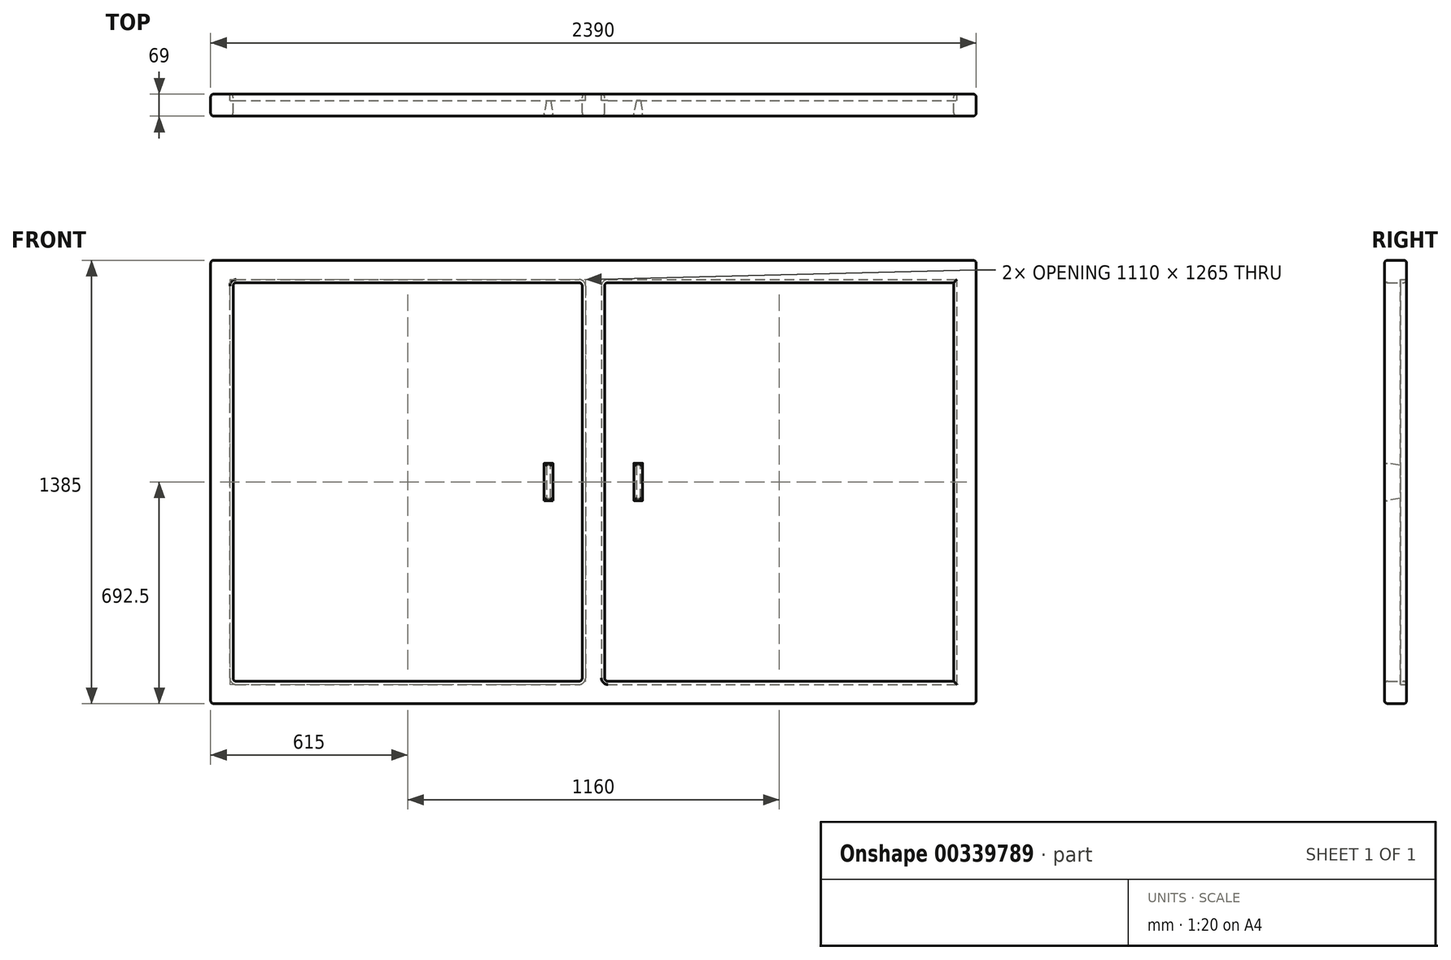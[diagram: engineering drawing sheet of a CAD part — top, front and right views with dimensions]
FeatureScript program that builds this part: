
annotation { "Feature Type Name" : "Feature", "Feature Type Description" : "" }
export const myFeature = defineFeature(function(context is Context, id is Id, definition is map)
    precondition{}
    {
        {
            var Q0;
            Q0=qCreatedBy(makeId("Front.planeOp"),FACE);
            var sketch = newSketch(context, id + "F0", { "sketchPlane" : qUnion([Q0])});
            skLineSegment(sketch, "E0.bottom", {"start": v(0, 0) * mm, "end": v(2390, 0) * mm});
            skLineSegment(sketch, "E0.top", {"start": v(0, 1385) * mm, "end": v(2390, 1385) * mm});
            skLineSegment(sketch, "E0.left", {"start": v(0, 0) * mm, "end": v(0, 1385) * mm});
            skLineSegment(sketch, "E0.right", {"start": v(2390, 0) * mm, "end": v(2390, 1385) * mm});
            skLineSegment(sketch, "E1.0", {"start": v(70, 1315) * mm, "end": v(1160, 1315) * mm});
            skLineSegment(sketch, "E1.1", {"start": v(70, 70) * mm, "end": v(70, 1315) * mm});
            skLineSegment(sketch, "E1.2", {"start": v(70, 70) * mm, "end": v(1160, 70) * mm});
            skLineSegment(sketch, "E1.3", {"start": v(2320, 70) * mm, "end": v(2320, 1315) * mm});
            skLineSegment(sketch, "E2.0", {"start": v(1160, 1315) * mm, "end": v(1160, 70) * mm});
            skLineSegment(sketch, "E3.0", {"start": v(1230, 1315) * mm, "end": v(1230, 70) * mm});
            skPoint(sketch, "E4.end.orphan", {"position": v(1195, 70) * mm});
            skPoint(sketch, "E4.start.orphan", {"position": v(1195, 1315) * mm});
            skLineSegment(sketch, "E5.trimOffspring", {"start": v(1230, 1315) * mm, "end": v(2320, 1315) * mm});
            skLineSegment(sketch, "E6.trimOffspring", {"start": v(1230, 70) * mm, "end": v(2320, 70) * mm});
            skSolve(sketch);
        }
        {
            var Q0;
            Q0=makeQuery(id+"F0.imprint","IMPRINT",FACE,{"disambiguationData":[TD([[makeQuery(id+"F0.imprint","IMPRINT",EDGE,{"derivedFrom":sQuery(id+"F0.wireOp",EDGE,"E0.bottom")}),1.0]])]});
            extrude(context, id + "F1", {"entities" : qUnion([Q0]), "depth" : 69 * mm});
        }
        {
            var Q0;
            Q0=makeQuery(id+"F1.opExtrude","CAP_FACE",FACE,{"disambiguationData":[OSD([sQuery(id+"F0.wireOp",EDGE,"E0.bottom"),sQuery(id+"F0.wireOp",EDGE,"E0.top"),sQuery(id+"F0.wireOp",EDGE,"E0.left"),sQuery(id+"F0.wireOp",EDGE,"E0.right"),sQuery(id+"F0.wireOp",EDGE,"E1.0"),sQuery(id+"F0.wireOp",EDGE,"E1.1"),sQuery(id+"F0.wireOp",EDGE,"E1.2"),sQuery(id+"F0.wireOp",EDGE,"E1.3"),sQuery(id+"F0.wireOp",EDGE,"E2.0"),sQuery(id+"F0.wireOp",EDGE,"E3.0"),sQuery(id+"F0.wireOp",EDGE,"E5.trimOffspring"),sQuery(id+"F0.wireOp",EDGE,"E6.trimOffspring")])],"isStart":false});
            var Q1;
            Q1=makeQuery(id+"F1.opExtrude","CAP_FACE",FACE,{"disambiguationData":[OSD([sQuery(id+"F0.wireOp",EDGE,"E0.bottom"),sQuery(id+"F0.wireOp",EDGE,"E0.top"),sQuery(id+"F0.wireOp",EDGE,"E0.left"),sQuery(id+"F0.wireOp",EDGE,"E0.right"),sQuery(id+"F0.wireOp",EDGE,"E1.0"),sQuery(id+"F0.wireOp",EDGE,"E1.1"),sQuery(id+"F0.wireOp",EDGE,"E1.2"),sQuery(id+"F0.wireOp",EDGE,"E1.3"),sQuery(id+"F0.wireOp",EDGE,"E2.0"),sQuery(id+"F0.wireOp",EDGE,"E3.0"),sQuery(id+"F0.wireOp",EDGE,"E5.trimOffspring"),sQuery(id+"F0.wireOp",EDGE,"E6.trimOffspring")])],"isStart":true});
            var Q2;
            Q2=makeQuery(id+"F1.opExtrude","SWEPT_FACE",FACE,{"disambiguationData":[OSD([sQuery(id+"F0.wireOp",EDGE,"E0.top")])]});
            var Q3;
            Q3=makeQuery(id+"F1.opExtrude","SWEPT_FACE",FACE,{"disambiguationData":[OSD([sQuery(id+"F0.wireOp",EDGE,"E0.right")])]});
            var Q4;
            Q4=makeQuery(id+"F1.opExtrude","SWEPT_FACE",FACE,{"disambiguationData":[OSD([sQuery(id+"F0.wireOp",EDGE,"E1.2")])]});
            var Q5;
            Q5=makeQuery(id+"F1.opExtrude","SWEPT_FACE",FACE,{"disambiguationData":[OSD([sQuery(id+"F0.wireOp",EDGE,"E3.0")])]});
            var Q6;
            Q6=makeQuery(id+"F1.opExtrude","SWEPT_FACE",FACE,{"disambiguationData":[OSD([sQuery(id+"F0.wireOp",EDGE,"E0.bottom")])]});
            var Q7;
            Q7=makeQuery(id+"F1.opExtrude","SWEPT_EDGE",EDGE,{"disambiguationData":[OSD([sQuery(id+"F0.wireOp",EDGE,"E1.0"),sQuery(id+"F0.wireOp",EDGE,"E2.0")])]});
            var Q8;
            Q8=makeQuery(id+"F1.opExtrude","SWEPT_EDGE",EDGE,{"disambiguationData":[OSD([sQuery(id+"F0.wireOp",EDGE,"E1.0"),sQuery(id+"F0.wireOp",EDGE,"E1.1")])]});
            fillet(context, id + "F2", {"entities" : qUnion([Q0, Q1, Q2, Q3, Q4, Q5, Q6, Q7, Q8]), "radius" : 10 * mm, "tangentPropagation" : true, "allowEdgeOverflow" : false});
        }
        {
            var Q0;
            Q0=qCreatedBy(makeId("Front.planeOp"),FACE);
            var sketch = newSketch(context, id + "F3", { "sketchPlane" : qUnion([Q0])});
            skLineSegment(sketch, "E7.0", {"start": v(1320, 632.5) * mm, "end": v(1320, 752.5) * mm});
            skLineSegment(sketch, "E8", {"start": v(1320, 692.5) * mm, "end": v(1320, 752.5) * mm});
            skLineSegment(sketch, "E9", {"start": v(1320, 752.5) * mm, "end": v(1350, 752.5) * mm});
            skLineSegment(sketch, "E10", {"start": v(1350, 752.5) * mm, "end": v(1350, 632.5) * mm});
            skLineSegment(sketch, "E11", {"start": v(1350, 632.5) * mm, "end": v(1320, 632.5) * mm});
            skLineSegment(sketch, "E12.0", {"start": v(5, 5) * mm, "end": v(2385, 5) * mm});
            skLineSegment(sketch, "E12.1", {"start": v(5, 1380) * mm, "end": v(5, 5) * mm});
            skLineSegment(sketch, "E12.2", {"start": v(2385, 1380) * mm, "end": v(5, 1380) * mm});
            skLineSegment(sketch, "E12.3", {"start": v(2385, 5) * mm, "end": v(2385, 1380) * mm});
            skLineSegment(sketch, "E13.0", {"start": v(1195, 1305) * mm, "end": v(1195, 80) * mm});
            skPoint(sketch, "E14.orphan", {"position": v(1320, 1305) * mm});
            skPoint(sketch, "E15.orphan", {"position": v(1320, 80) * mm});
            skLineSegment(sketch, "E16.MirrorCS", {"start": v(1070, 692.5) * mm, "end": v(1070, 752.5) * mm});
            skLineSegment(sketch, "E17.MirrorCS", {"start": v(1070, 632.5) * mm, "end": v(1070, 752.5) * mm});
            skLineSegment(sketch, "E18.MirrorCS", {"start": v(1040, 632.5) * mm, "end": v(1070, 632.5) * mm});
            skLineSegment(sketch, "E19.MirrorCS", {"start": v(1040, 752.5) * mm, "end": v(1040, 632.5) * mm});
            skLineSegment(sketch, "E20.MirrorCS", {"start": v(1070, 752.5) * mm, "end": v(1040, 752.5) * mm});
            skSolve(sketch);
        }
        {
            var Q0;
            Q0=makeQuery(id+"F1.opExtrude","CAP_FACE",FACE,{"disambiguationData":[OSD([sQuery(id+"F0.wireOp",EDGE,"E0.bottom"),sQuery(id+"F0.wireOp",EDGE,"E0.top"),sQuery(id+"F0.wireOp",EDGE,"E0.left"),sQuery(id+"F0.wireOp",EDGE,"E0.right"),sQuery(id+"F0.wireOp",EDGE,"E1.0"),sQuery(id+"F0.wireOp",EDGE,"E1.1"),sQuery(id+"F0.wireOp",EDGE,"E1.2"),sQuery(id+"F0.wireOp",EDGE,"E1.3"),sQuery(id+"F0.wireOp",EDGE,"E2.0"),sQuery(id+"F0.wireOp",EDGE,"E3.0"),sQuery(id+"F0.wireOp",EDGE,"E5.trimOffspring"),sQuery(id+"F0.wireOp",EDGE,"E6.trimOffspring")])],"isStart":true});
            var sketch = newSketch(context, id + "F4", { "sketchPlane" : qUnion([Q0])});
            skLineSegment(sketch, "E21.0", {"start": v(-2330, 60) * mm, "end": v(-2330, 1325) * mm});
            skArc(sketch, "E21.1", {"start": v(-1220, 1305) * mm, "mid": v(-1225.86, 1319.14) * mm, "end": v(-1240, 1325) * mm});
            skLineSegment(sketch, "E21.2", {"start": v(-1220, 1305) * mm, "end": v(-1220, 80) * mm});
            skLineSegment(sketch, "E21.3", {"start": v(-2330, 1325) * mm, "end": v(-1240, 1325) * mm});
            skArc(sketch, "E21.4", {"start": v(-1240, 60) * mm, "mid": v(-1225.86, 65.86) * mm, "end": v(-1220, 80) * mm});
            skLineSegment(sketch, "E21.5", {"start": v(-1240, 60) * mm, "end": v(-2330, 60) * mm});
            skArc(sketch, "E22.0", {"start": v(-1150, 1325) * mm, "mid": v(-1164.14, 1319.14) * mm, "end": v(-1170, 1305) * mm});
            skLineSegment(sketch, "E22.1", {"start": v(-1170, 80) * mm, "end": v(-1170, 1305) * mm});
            skLineSegment(sketch, "E22.2", {"start": v(-1150, 1325) * mm, "end": v(-80, 1325) * mm});
            skArc(sketch, "E22.3", {"start": v(-1170, 80) * mm, "mid": v(-1164.14, 65.86) * mm, "end": v(-1150, 60) * mm});
            skArc(sketch, "E22.4", {"start": v(-60, 1305) * mm, "mid": v(-65.86, 1319.14) * mm, "end": v(-80, 1325) * mm});
            skLineSegment(sketch, "E22.5", {"start": v(-60, 1305) * mm, "end": v(-60, 80) * mm});
            skArc(sketch, "E22.6", {"start": v(-80, 60) * mm, "mid": v(-65.86, 65.86) * mm, "end": v(-60, 80) * mm});
            skLineSegment(sketch, "E22.7", {"start": v(-80, 60) * mm, "end": v(-1150, 60) * mm});
            skSolve(sketch);
        }
        {
            var Q0;
            Q0 = qSketchRegion(id + "F4", true);
            extrude(context, id + "F5", {"entities" : qUnion([Q0]), "oppositeDirection" : true, "depth" : 20 * mm});
        }
        {
            var Q0;
            Q0=makeQuery(id+"F1.opExtrude","CAP_FACE",FACE,{"disambiguationData":[OSD([sQuery(id+"F0.wireOp",EDGE,"E0.bottom"),sQuery(id+"F0.wireOp",EDGE,"E0.top"),sQuery(id+"F0.wireOp",EDGE,"E0.left"),sQuery(id+"F0.wireOp",EDGE,"E0.right"),sQuery(id+"F0.wireOp",EDGE,"E1.0"),sQuery(id+"F0.wireOp",EDGE,"E1.1"),sQuery(id+"F0.wireOp",EDGE,"E1.2"),sQuery(id+"F0.wireOp",EDGE,"E1.3"),sQuery(id+"F0.wireOp",EDGE,"E2.0"),sQuery(id+"F0.wireOp",EDGE,"E3.0"),sQuery(id+"F0.wireOp",EDGE,"E5.trimOffspring"),sQuery(id+"F0.wireOp",EDGE,"E6.trimOffspring")])],"isStart":false});
            var sketch = newSketch(context, id + "F6", { "sketchPlane" : qUnion([Q0])});
            skLineSegment(sketch, "E23.0", {"start": v(1350, 632.5) * mm, "end": v(1350, 752.5) * mm});
            skLineSegment(sketch, "E23.1", {"start": v(1320, 632.5) * mm, "end": v(1350, 632.5) * mm});
            skLineSegment(sketch, "E23.2", {"start": v(1350, 752.5) * mm, "end": v(1320, 752.5) * mm});
            skLineSegment(sketch, "E23.3", {"start": v(1320, 752.5) * mm, "end": v(1320, 692.5) * mm});
            skLineSegment(sketch, "E23.4", {"start": v(1320, 692.5) * mm, "end": v(1320, 632.5) * mm});
            skLineSegment(sketch, "E24.0", {"start": v(1070, 752.5) * mm, "end": v(1040, 752.5) * mm});
            skLineSegment(sketch, "E24.1", {"start": v(1070, 692.5) * mm, "end": v(1070, 752.5) * mm});
            skLineSegment(sketch, "E24.2", {"start": v(1040, 752.5) * mm, "end": v(1040, 632.5) * mm});
            skLineSegment(sketch, "E24.3", {"start": v(1040, 632.5) * mm, "end": v(1070, 632.5) * mm});
            skLineSegment(sketch, "E24.4", {"start": v(1070, 632.5) * mm, "end": v(1070, 692.5) * mm});
            skSolve(sketch);
        }
        {
            var Q0;
            Q0=makeQuery(id+"F6.imprint","IMPRINT",FACE,{"disambiguationData":[TD([[makeQuery(id+"F6.imprint","IMPRINT",EDGE,{"derivedFrom":sQuery(id+"F6.wireOp",EDGE,"E24.0")}),1.0]])]});
            var Q1;
            Q1=makeQuery(id+"F6.imprint","IMPRINT",FACE,{"disambiguationData":[TD([[makeQuery(id+"F6.imprint","IMPRINT",EDGE,{"derivedFrom":sQuery(id+"F6.wireOp",EDGE,"E23.0")}),1.0]])]});
            extrude(context, id + "F7", {"entities" : qUnion([Q0, Q1]), "endBound" : BoundingType.UP_TO_NEXT, "oppositeDirection" : true, "depth" : 25 * mm, "hasDraft" : true, "draftAngle" : 10 * degree, "draftPullDirection" : true});
        }
        {
            var Q0;
            Q0=makeQuery(id+"F7.opExtrude","CAP_FACE",FACE,{"disambiguationData":[OSD([sQuery(id+"F6.wireOp",EDGE,"E23.0"),sQuery(id+"F6.wireOp",EDGE,"E23.1"),sQuery(id+"F6.wireOp",EDGE,"E23.2"),sQuery(id+"F6.wireOp",EDGE,"E23.3"),sQuery(id+"F6.wireOp",EDGE,"E23.4")])],"isStart":true});
            var Q1;
            Q1=makeQuery(id+"F7.opExtrude","CAP_FACE",FACE,{"disambiguationData":[OSD([sQuery(id+"F6.wireOp",EDGE,"E24.0"),sQuery(id+"F6.wireOp",EDGE,"E24.1"),sQuery(id+"F6.wireOp",EDGE,"E24.2"),sQuery(id+"F6.wireOp",EDGE,"E24.3"),sQuery(id+"F6.wireOp",EDGE,"E24.4")])],"isStart":true});
            fillet(context, id + "F8", {"entities" : qUnion([Q0, Q1]), "radius" : 7.5 * mm, "tangentPropagation" : true, "allowEdgeOverflow" : false});
        }
    });
